# Revit family: Faucet-Deck_Mounted-Waterworks-Flyte-Three_Hole
name_source: partatom
category: Plumbing Fixtures
revit_build: Autodesk Revit MEP 2014 (Build: 20140709_2115(x64)
units: mm (PartAtom-declared; Revit-internal decimal feet)

## types (1)
- Not A Type - Load Type Catalog
    ADA Compliant = Yes
    Anti-scald Protection = No
    Assembly Code = D2010
    CW Connection = Yes
    CWFU = 0
    Certification CEC = Yes
    Certification IAPMO = Yes
    Certification NSF = Yes
    Certification State of MA = Yes
    Certification Watersense = Yes
    Certification cUPC = Yes
    Code Compliance = Code # FLLS01: CEC, Watersense
    Cold Water Connector = Cold Water - Male with Supply Nut
    Cold Water Diameter = 0' - 0 1/2"
    Constraint = 1
    ControlM = 1
    Cross Handles = Yes
    Default Elevation = 2' - 10"
    Depth = 0' - 7 5/8"
    Description = Flyte Low Profile Three Hole Deck Mounted Lavatory Faucet with Metal Cross Handles in Chrome, 1.2gpm, Fixed Spray
    Domestic Water Flow Rate = 1 GPM
    Finish = Metal - Waterworks - Chrome
    Fittings Hole Diameter = 0' - 1 3/8"
    HW Connection = Yes
    HWFU = 0
    Height = 0' - 4 1/8"
    Hot Limit Safety Stop = No
    Hot Water Connector = Hot Water - Male with Supply Nut
    Hot Water Diameter = 0' - 0 1/2"
    Keynote = 22 40 00
    Lever Handles = No
    Manufacturer = Waterworks
    Model = FLLS01
    Model SKU = 07-12419-82097
    Pressure = 45.00 psi
    Product Documentation Link = http://assets.waterworks.com
    Product Name = Flyte Low Profile Three Hole Deck Mounted Lavatory Faucet with Metal Lever Handles
    Product Page URL = http://www.waterworks.com
    Spout Reach = 0' - 6"
    URL = http://www.waterworks.com
    Valve Material = Ceramic
    Vent Connection = No
    Version = 2014 - v1.0a
    WFU = 0
    Warranty = http://www.waterworks.com
    Waste Connection = No
    Water Pressure = Max: 85psi / Min: 20psi / Recommended: 45psi
    ‌Installation Requirements or Notes = Standard flow rate is 1.5gpm (5.7 L/min) and State of California requires 1.2gpm(4.5 L/min).

## geometry (parser evidence)
native form markers: Sweep x1
no freeform markers — native parametric forms only
